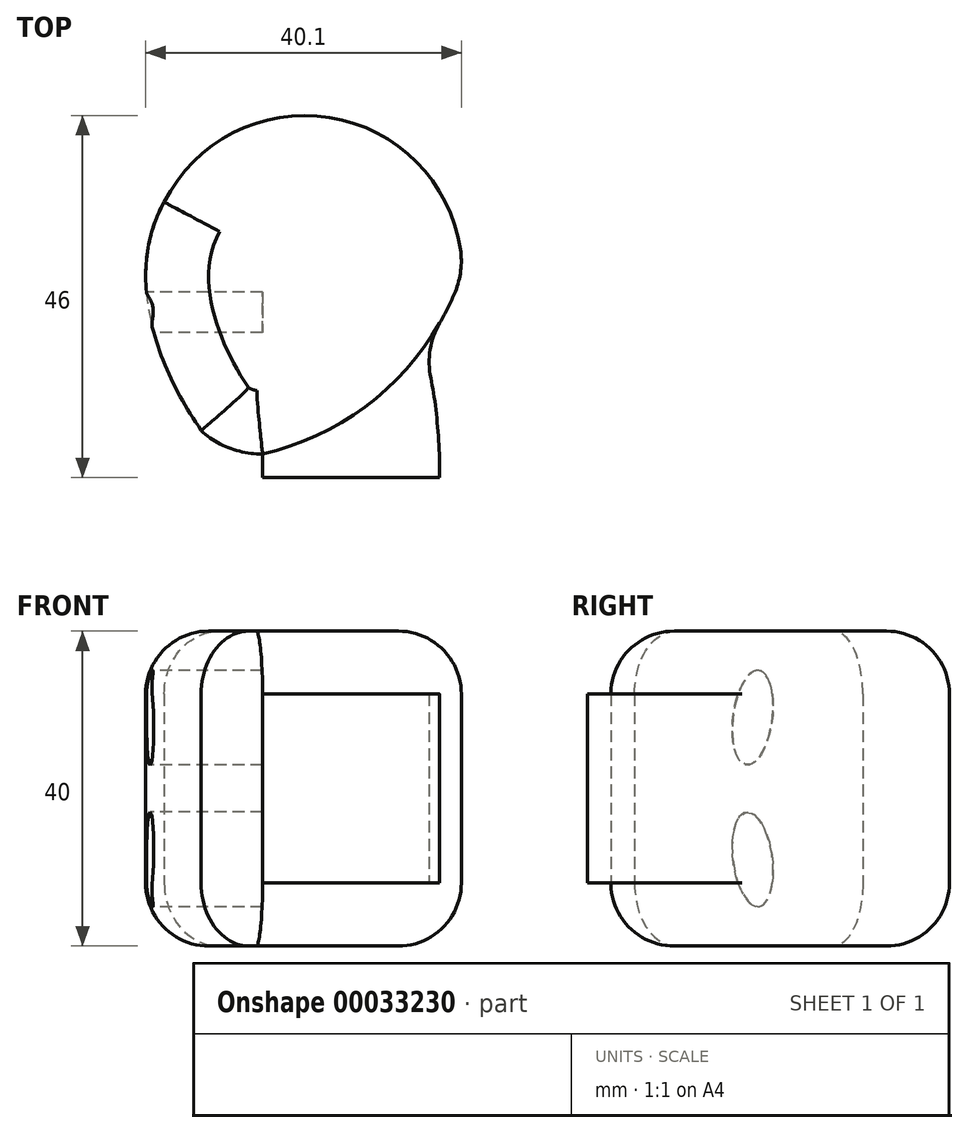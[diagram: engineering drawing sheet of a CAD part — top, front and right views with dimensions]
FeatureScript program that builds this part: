
annotation { "Feature Type Name" : "Feature", "Feature Type Description" : "" }
export const myFeature = defineFeature(function(context is Context, id is Id, definition is map)
    precondition{}
    {
        {
            var Q0;
            Q0=qCreatedBy(makeId("Top.planeOp"),FACE);
            var sketch = newSketch(context, id + "F0", { "sketchPlane" : qUnion([Q0])});
            skEllipticalArc(sketch, "E0", {});
            skLineSegment(sketch, "E1", {"start": v(-7.8, -5) * mm, "end": v(0, -5) * mm, "construction": true});
            skLineSegment(sketch, "E2", {"start": v(0, -5) * mm, "end": v(0, -8) * mm, "construction": true});
            skPoint(sketch, "E3.start.orphan", {"position": v(-10, 0) * mm});
            skEllipticalArc(sketch, "E4", {});
            skPoint(sketch, "E5", {"position": v(-12.5, 24) * mm});
            skEllipticalArc(sketch, "E6", {});
            skPoint(sketch, "E7", {"position": v(5.36, 35) * mm});
            skPoint(sketch, "E8", {"position": v(25.36, 15) * mm});
            skEllipticalArc(sketch, "E9.trimOffspring", {});
            skArc(sketch, "E10", {"start": v(0, -8) * mm, "mid": v(15.68, 0.19) * mm, "end": v(25.36, 15) * mm});
            const initialGuessF0  = {"E0": [0, 0, 0, 1, 0.008, 0.01, 2.245927859731882, 3.141592653589793], "E4": [0.03219375250200172, -0.001, -0.8727431764748058, 0.48817962669151427, 0.05121065819446363, 0.030073461642533206, 0, 0.8716590437257873], "E6": [0.005360571099491888, 0.015, 0, 1, 0.02, 0.02, 1.1040309877476178, 3.141592653589793], "E9.trimOffspring": [0.005360571099491888, 0.015, 0, 1, 0.02, 0.02, 4.71238898038469, 1.104030987747615]};
            skSetInitialGuess(sketch, initialGuessF0);
            skSolve(sketch);
        }
        {
            var Q0;
            Q0 = qSketchRegion(id + "F0", true);
            extrude(context, id + "F1", {"entities" : qUnion([Q0]), "depth" : 20 * mm, "hasSecondDirection" : true, "secondDirectionOppositeDirection" : true, "secondDirectionDepth" : 20 * mm});
        }
        {
            var Q0;
            Q0=makeQuery(id+"F1.opExtrude","CAP_FACE",FACE,{"disambiguationData":[OSD([sQuery(id+"F0.wireOp",EDGE,"E0"),sQuery(id+"F0.wireOp",EDGE,"E4"),sQuery(id+"F0.wireOp",EDGE,"E9.trimOffspring"),sQuery(id+"F0.wireOp",EDGE,"E10")])],"isStart":false});
            var Q1;
            Q1=makeQuery(id+"F1.opExtrude","CAP_FACE",FACE,{"disambiguationData":[OSD([sQuery(id+"F0.wireOp",EDGE,"E0"),sQuery(id+"F0.wireOp",EDGE,"E4"),sQuery(id+"F0.wireOp",EDGE,"E9.trimOffspring"),sQuery(id+"F0.wireOp",EDGE,"E10")])],"isStart":true});
            fillet(context, id + "F2", {"entities" : qUnion([Q0, Q1]), "radius" : 8 * mm, "tangentPropagation" : true, "allowEdgeOverflow" : false});
        }
        {
            var Q0;
            Q0=qCreatedBy(makeId("Right.planeOp"),FACE);
            var sketch = newSketch(context, id + "F3", { "sketchPlane" : qUnion([Q0])});
            skCircle(sketch, "E11", {"center": v(10, -9) * mm, "radius": 4 * mm, "construction": true});
            skCircle(sketch, "E12.MirrorC", {"center": v(10, 9) * mm, "radius": 4 * mm, "construction": true});
            skEllipse(sketch, "E13", {"center": v(10, -9) * mm, "majorRadius": 6.05 * mm, "minorRadius": 2.5 * mm, "majorAxis": v(0.13, -1)});
            skPoint(sketch, "E14", {"position": v(12.48, -8.67) * mm});
            skPoint(sketch, "E15", {"position": v(9.21, -3) * mm});
            skLineSegment(sketch, "E16", {"start": v(9.21, -3) * mm, "end": v(10.79, -15) * mm, "construction": true});
            skEllipse(sketch, "E17.MirrorC", {"center": v(10, 9) * mm, "majorRadius": 6.05 * mm, "minorRadius": 2.5 * mm, "majorAxis": v(0.13, 1)});
            skSolve(sketch);
        }
        {
            var Q0;
            Q0 = qSketchRegion(id + "F3", true);
            extrude(context, id + "F4", {"entities" : qUnion([Q0]), "operationType" : NewBodyOperationType.REMOVE, "endBound" : BoundingType.UP_TO_NEXT, "oppositeDirection" : true, "depth" : 25 * mm});
        }
        {
            var Q0;
            Q0=qCreatedBy(makeId("Top.planeOp"),FACE);
            var sketch = newSketch(context, id + "F5", { "sketchPlane" : qUnion([Q0])});
            skLineSegment(sketch, "E18", {"start": v(0, 0) * mm, "end": v(0, -11) * mm});
            skLineSegment(sketch, "E19", {"start": v(0, -11) * mm, "end": v(22.5, -11) * mm});
            skEllipticalArc(sketch, "E20", {});
            skPoint(sketch, "E21", {"position": v(17.5, 9) * mm});
            skLineSegment(sketch, "E22", {"start": v(17.5, 9) * mm, "end": v(0, 0) * mm});
            const initialGuessF5  = {"E20": [0.0175, -0.011, 1, 0, 0.005, 0.02, 6.283185307179586, 1.5707963267948966]};
            skSetInitialGuess(sketch, initialGuessF5);
            skSolve(sketch);
        }
        {
            var Q0;
            Q0 = qSketchRegion(id + "F5", true);
            extrude(context, id + "F6", {"entities" : qUnion([Q0]), "operationType" : NewBodyOperationType.ADD, "depth" : 12 * mm, "hasSecondDirection" : true, "secondDirectionOppositeDirection" : true, "secondDirectionDepth" : 12 * mm});
        }
        {
            var Q0;
            Q0=makeQuery(id+"F1.opExtrude","SWEPT_EDGE",EDGE,{"disambiguationData":[OSD([sQuery(id+"F0.wireOp",EDGE,"E9.trimOffspring"),sQuery(id+"F0.wireOp",EDGE,"E10")])]});
            var Q1;
            Q1=makeQuery(id+"F6.boolean.opBoolean","INTERSECT",EDGE,{"derivedFrom":[makeQuery(id+"F1.opExtrude","SWEPT_FACE",FACE,{"disambiguationData":[OSD([sQuery(id+"F0.wireOp",EDGE,"E10")])]}),makeQuery(id+"F6.opExtrude","SWEPT_FACE",FACE,{"disambiguationData":[OSD([sQuery(id+"F5.wireOp",EDGE,"E20")])]})]});
            fillet(context, id + "F7", {"entities" : qUnion([Q0, Q1]), "radius" : 10 * mm, "tangentPropagation" : true, "allowEdgeOverflow" : false});
        }
    });
